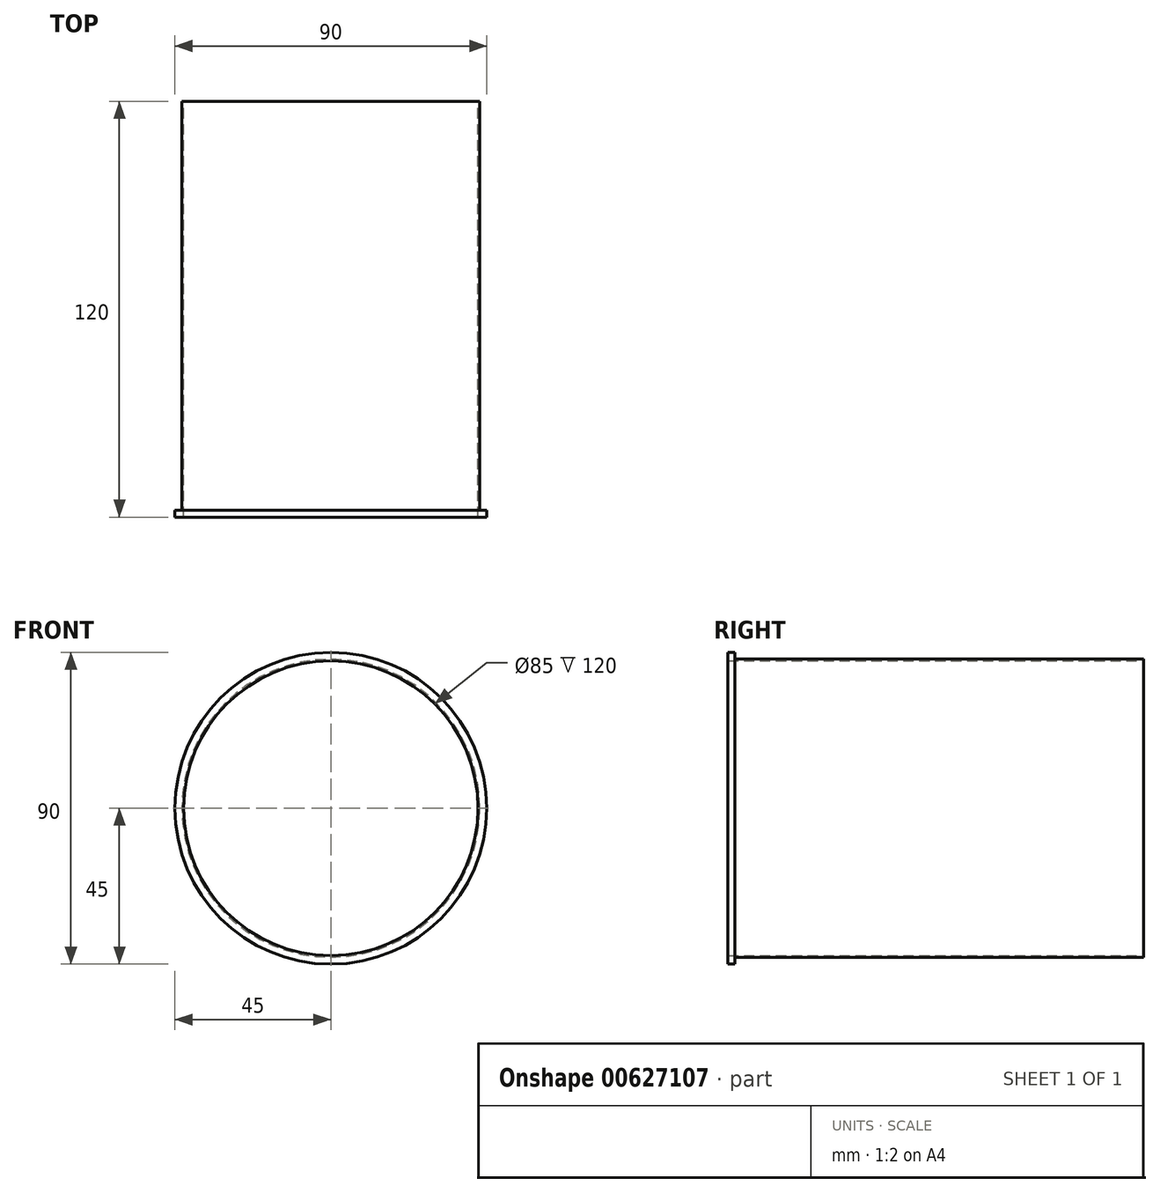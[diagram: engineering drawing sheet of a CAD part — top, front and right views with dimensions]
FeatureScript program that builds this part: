
annotation { "Feature Type Name" : "Feature", "Feature Type Description" : "" }
export const myFeature = defineFeature(function(context is Context, id is Id, definition is map)
    precondition{}
    {
        {
            var Q0;
            Q0=qCreatedBy(makeId("Front.planeOp"),FACE);
            var sketch = newSketch(context, id + "F0", { "sketchPlane" : qUnion([Q0])});
            skCircle(sketch, "E0", {"center": v(0, 0) * mm, "radius": 42.5 * mm});
            skCircle(sketch, "E1.0", {"center": v(0, 0) * mm, "radius": 43 * mm});
            skSolve(sketch);
        }
        {
            var Q0;
            Q0 = qSketchRegion(id + "F0", true);
            extrude(context, id + "F1", {"entities" : qUnion([Q0]), "depth" : 118 * mm, "offsetDistance" : 25 * mm});
        }
        {
            var Q0;
            Q0=makeQuery(id+"F1.opExtrude","CAP_FACE",FACE,{"disambiguationData":[OSD([sQuery(id+"F0.wireOp",EDGE,"E0"),sQuery(id+"F0.wireOp",EDGE,"E1.0")])],"isStart":false});
            var sketch = newSketch(context, id + "F2", { "sketchPlane" : qUnion([Q0])});
            skCircle(sketch, "E2", {"center": v(0, 0) * mm, "radius": 45 * mm});
            skCircle(sketch, "E3.0", {"center": v(0, 0) * mm, "radius": 42.5 * mm});
            skSolve(sketch);
        }
        {
            var Q0;
            Q0 = qSketchRegion(id + "F2", true);
            extrude(context, id + "F3", {"entities" : qUnion([Q0]), "operationType" : NewBodyOperationType.ADD, "depth" : 2 * mm, "offsetDistance" : 25 * mm});
        }
    });
